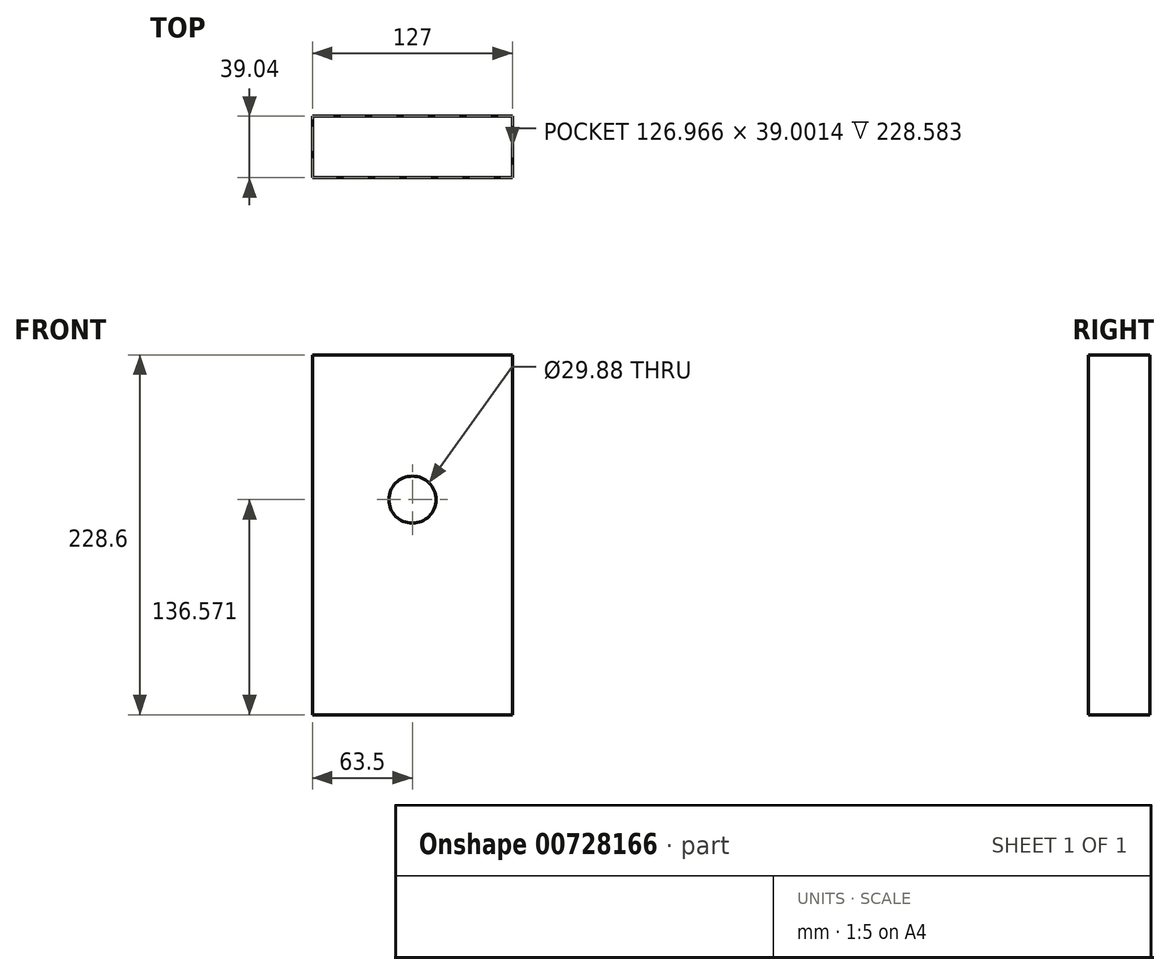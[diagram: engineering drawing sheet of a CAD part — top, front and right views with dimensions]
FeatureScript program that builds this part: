
annotation { "Feature Type Name" : "Feature", "Feature Type Description" : "" }
export const myFeature = defineFeature(function(context is Context, id is Id, definition is map)
    precondition{}
    {
        {
            var Q0;
            Q0=qCreatedBy(makeId("Top.planeOp"),FACE);
            var sketch = newSketch(context, id + "F0", { "sketchPlane" : qUnion([Q0])});
            skLineSegment(sketch, "E0.bottom", {"start": v(63.5, 19.52) * mm, "end": v(-63.5, 19.52) * mm});
            skLineSegment(sketch, "E0.top", {"start": v(63.5, -19.52) * mm, "end": v(-63.5, -19.52) * mm});
            skLineSegment(sketch, "E0.left", {"start": v(63.5, 19.52) * mm, "end": v(63.5, -19.52) * mm});
            skLineSegment(sketch, "E0.right", {"start": v(-63.5, 19.52) * mm, "end": v(-63.5, -19.52) * mm});
            skPoint(sketch, "E0.middle", {"position": v(0, 0) * mm});
            skSolve(sketch);
        }
        {
            var Q0;
            Q0 = qSketchRegion(id + "F0", true);
            extrude(context, id + "F1", {"entities" : qUnion([Q0]), "depth" : 228.6 * mm, "offsetDistance" : 25.4 * mm});
        }
        {
            var Q0;
            Q0=makeQuery(id+"F1.opExtrude","CAP_FACE",FACE,{"disambiguationData":[OSD([sQuery(id+"F0.wireOp",EDGE,"E0.bottom"),sQuery(id+"F0.wireOp",EDGE,"E0.top"),sQuery(id+"F0.wireOp",EDGE,"E0.left"),sQuery(id+"F0.wireOp",EDGE,"E0.right")])],"isStart":false});
            shell(context, id + "F2", {"entities" : qUnion([Q0]), "thickness" : 3 / 177.8 * mm});
        }
        {
            var Q0;
            Q0=makeQuery(id+"F1.opExtrude","SWEPT_FACE",FACE,{"disambiguationData":[OSD([sQuery(id+"F0.wireOp",EDGE,"E0.top")])]});
            var sketch = newSketch(context, id + "F3", { "sketchPlane" : qUnion([Q0])});
            skCircle(sketch, "E1", {"center": v(0, 136.57) * mm, "radius": 14.94 * mm});
            skSolve(sketch);
        }
        {
            var Q0;
            Q0 = qSketchRegion(id + "F3", true);
            extrude(context, id + "F4", {"entities" : qUnion([Q0]), "operationType" : NewBodyOperationType.REMOVE, "oppositeDirection" : true, "depth" : 0.08 * mm, "offsetDistance" : 25.4 * mm});
        }
    });
